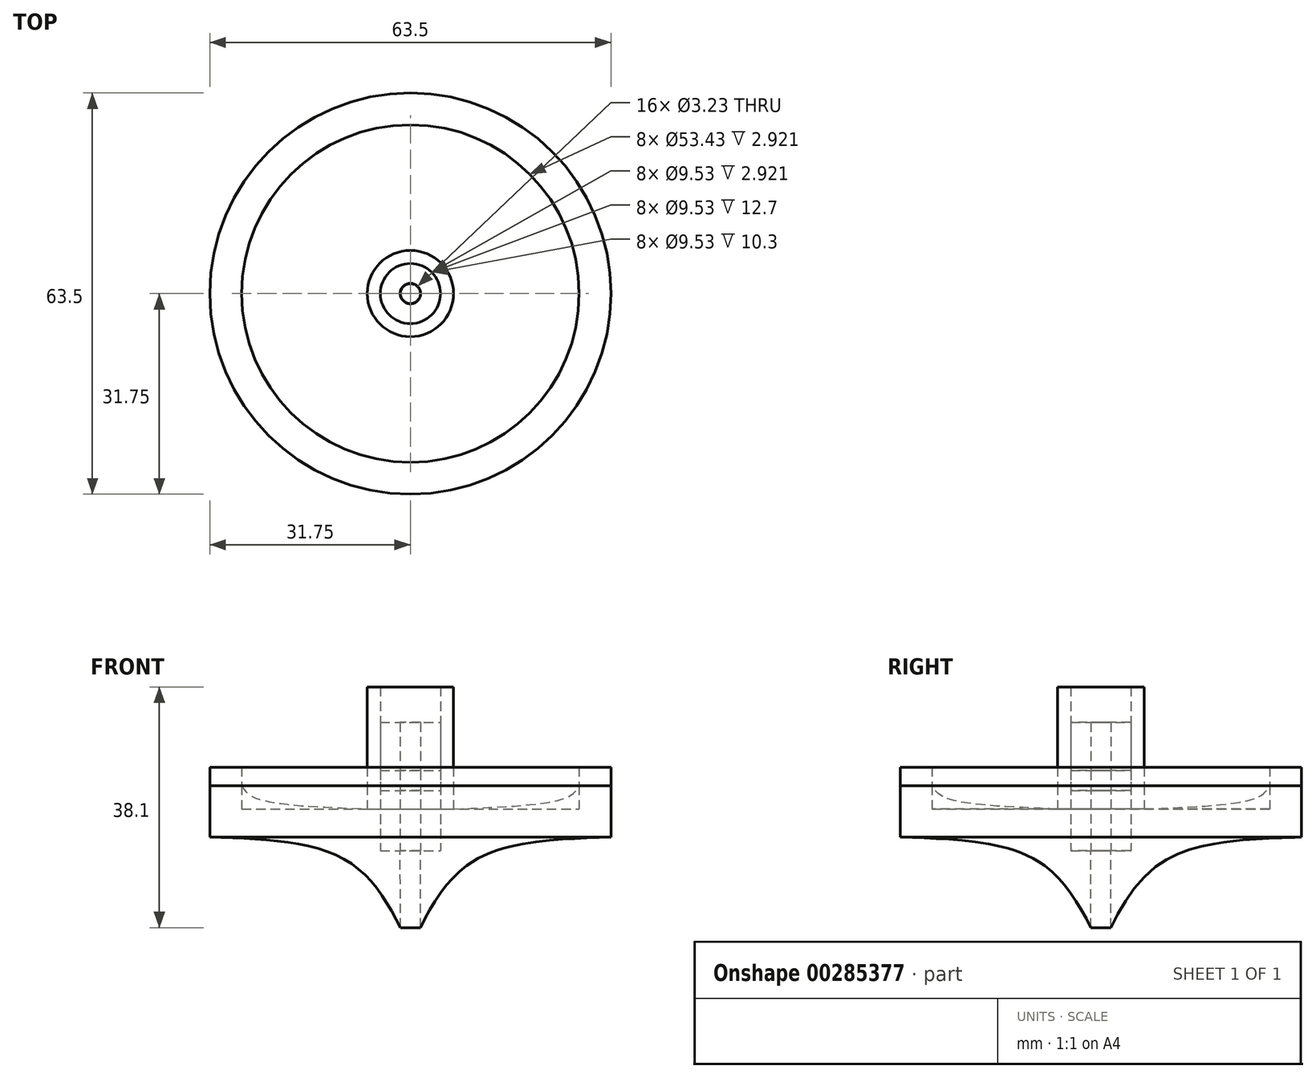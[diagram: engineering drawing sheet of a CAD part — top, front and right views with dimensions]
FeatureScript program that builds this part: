
annotation { "Feature Type Name" : "Feature", "Feature Type Description" : "" }
export const myFeature = defineFeature(function(context is Context, id is Id, definition is map)
    precondition{}
    {
        {
            var Q0;
            Q0=qCreatedBy(makeId("Front.planeOp"),FACE);
            var sketch = newSketch(context, id + "F0", { "sketchPlane" : qUnion([Q0])});
            skLineSegment(sketch, "E0", {"start": v(0, 0) * mm, "end": v(31.75, 0) * mm});
            skLineSegment(sketch, "E1", {"start": v(31.75, 0) * mm, "end": v(31.75, 8.17) * mm});
            skLineSegment(sketch, "E2", {"start": v(31.75, 8.17) * mm, "end": v(26.72, 8.17) * mm});
            skLineSegment(sketch, "E3", {"start": v(0, 8.17) * mm, "end": v(0, 0) * mm});
            skLineSegment(sketch, "E4.MirrorCS", {"start": v(-31.75, 8.17) * mm, "end": v(-26.72, 8.17) * mm});
            skLineSegment(sketch, "E5.MirrorCS", {"start": v(0, 0) * mm, "end": v(-31.75, 0) * mm});
            skLineSegment(sketch, "E6.MirrorCS", {"start": v(-31.75, 0) * mm, "end": v(-31.75, 8.17) * mm});
            skPoint(sketch, "E7", {"position": v(-26.72, 8.17) * mm});
            skPoint(sketch, "E8", {"position": v(-26.72, 4.48) * mm});
            skLineSegment(sketch, "E9", {"start": v(-26.72, 8.17) * mm, "end": v(-26.72, 4.48) * mm});
            skLineSegment(sketch, "E10", {"start": v(-26.72, 4.48) * mm, "end": v(0, 4.48) * mm});
            skPoint(sketch, "E10.endSnap0", {"position": v(0, 4.09) * mm});
            skLineSegment(sketch, "E11", {"start": v(0, 4.48) * mm, "end": v(0, 8.17) * mm});
            skLineSegment(sketch, "E12.MirrorCS", {"start": v(26.72, 4.48) * mm, "end": v(0, 4.48) * mm});
            skPoint(sketch, "E13.MirrorP", {"position": v(26.72, 4.48) * mm});
            skLineSegment(sketch, "E14.MirrorCS", {"start": v(26.72, 8.17) * mm, "end": v(26.72, 4.48) * mm});
            skPoint(sketch, "E15.orphan", {"position": v(0, 8.17) * mm});
            skLineSegment(sketch, "E16", {"start": v(0, 4.48) * mm, "end": v(6.83, 4.48) * mm});
            skLineSegment(sketch, "E17", {"start": v(6.83, 4.48) * mm, "end": v(6.83, 8.17) * mm});
            skLineSegment(sketch, "E18", {"start": v(6.83, 8.17) * mm, "end": v(4.76, 8.17) * mm});
            skLineSegment(sketch, "E19", {"start": v(0, 4.48) * mm, "end": v(4.76, 4.48) * mm});
            skLineSegment(sketch, "E20", {"start": v(4.76, 4.48) * mm, "end": v(4.76, 8.17) * mm});
            skPoint(sketch, "E21.MirrorCS.start.orphan", {"position": v(-6.83, 8.17) * mm});
            skPoint(sketch, "E22.MirrorCS.start.orphan", {"position": v(-6.83, 4.48) * mm});
            skLineSegment(sketch, "E23.MirrorCS", {"start": v(-4.76, 4.48) * mm, "end": v(-4.76, 8.17) * mm});
            skLineSegment(sketch, "E24.MirrorCS", {"start": v(-6.83, 8.17) * mm, "end": v(-4.76, 8.17) * mm});
            skLineSegment(sketch, "E25.MirrorCS", {"start": v(-6.83, 4.48) * mm, "end": v(-6.83, 8.17) * mm});
            skFitSpline(sketch, "E26", {"points": [v(-26.72, 8.17) * mm, v(-24.89, 6.38) * mm, v(-6.83, 4.48) * mm], "startDerivative": vector(4.23, -7.1) * mm, "endDerivative": vector(31.44, -1.18) * mm});
            skFitSpline(sketch, "E27.MirrorCS", {"points": [v(26.72, 8.17) * mm, v(24.89, 6.38) * mm, v(6.83, 4.48) * mm], "startDerivative": vector(-4.23, -7.1) * mm, "endDerivative": vector(-31.44, -1.18) * mm});
            skLineSegment(sketch, "E28", {"start": v(0, 0) * mm, "end": v(1.68, 0) * mm});
            skLineSegment(sketch, "E29", {"start": v(0, 0) * mm, "end": v(1.57, 0) * mm});
            skFitSpline(sketch, "E30", {"points": [v(-31.75, 0) * mm, v(-9.83, -3.86) * mm, v(0, -17.56) * mm], "startDerivative": vector(46.32, -1.28) * mm, "endDerivative": vector(16.5, -34.6) * mm});
            skFitSpline(sketch, "E31.MirrorCS", {"points": [v(31.75, 0) * mm, v(9.83, -3.86) * mm, v(0, -17.56) * mm], "startDerivative": vector(-46.32, -1.28) * mm, "endDerivative": vector(-16.5, -34.6) * mm});
            skLineSegment(sketch, "E32", {"start": v(1.57, 0) * mm, "end": v(1.62, 0) * mm});
            skLineSegment(sketch, "E33.MirrorCS", {"start": v(-1.62, 0) * mm, "end": v(-1.57, -17.56) * mm});
            skPoint(sketch, "E34", {"position": v(1.58, -14.3) * mm});
            skPoint(sketch, "E35", {"position": v(0, -14.3) * mm});
            skSolve(sketch);
        }
        {
            var Q0;
            {var subQ0=sQuery(id+"F0.wireOp",EDGE,"E9");Q0=makeQuery(id+"F0.imprint","IMPRINT",FACE,{"disambiguationData":[TD([[makeQuery(id+"F0.imprint","IMPRINT",EDGE,{"derivedFrom":subQ0}),1.0]])]});}
            var Q1;
            {var subQ0=sQuery(id+"F0.wireOp",EDGE,"E23.MirrorCS");Q1=makeQuery(id+"F0.imprint","IMPRINT",FACE,{"disambiguationData":[TD([[makeQuery(id+"F0.imprint","IMPRINT",EDGE,{"derivedFrom":subQ0}),1.0]])]});}
            var Q2;
            Q2=makeQuery(id+"F0.imprint","IMPRINT",FACE,{"disambiguationData":[TD([[makeQuery(id+"F0.imprint","IMPRINT",EDGE,{"derivedFrom":sQuery(id+"F0.wireOp",EDGE,"E12.MirrorCS")}),-1.0]])]});
            var Q3;
            Q3=makeQuery(id+"F0.imprint","IMPRINT",FACE,{"disambiguationData":[TD([[makeQuery(id+"F0.imprint","IMPRINT",EDGE,{"derivedFrom":sQuery(id+"F0.wireOp",EDGE,"E16")}),1.0]])]});
            var Q4;
            {var subQ1=sQuery(id+"F0.wireOp",EDGE,"E5.MirrorCS");var subQ3=sQuery(id+"F0.wireOp",EDGE,"E33.MirrorCS");var subQ4=makeQuery(id+"F0.imprint","INTERSECT",VERTEX,{"derivedFrom":[subQ1,subQ3]});Q4=makeQuery(id+"F0.imprint","IMPRINT",FACE,{"disambiguationData":[TD([[makeQuery(id+"F0.imprint","IMPRINT",EDGE,{"disambiguationData":[TD([[subQ4,-1.0]])],"derivedFrom":subQ3}),-1.0]])]});}
            var Q5;
            {var subQ3=sQuery(id+"F0.wireOp",EDGE,"E3");Q5=makeQuery(id+"F0.imprint","IMPRINT",FACE,{"disambiguationData":[TD([[makeQuery(id+"F0.imprint","IMPRINT",EDGE,{"derivedFrom":subQ3}),-1.0]])]});}
            var Q6;
            Q6=sQuery(id+"F0.wireOp",EDGE,"E11");
            revolve(context, id + "F1", {"entities" : qUnion([Q0, Q1, Q2, Q3, Q4, Q5]), "axis" : qUnion([Q6]), "revolveType" : RevolveType.FULL});
        }
        {
            var Q0;
            Q0=makeQuery(id+"F1.opRevolve","SWEPT_FACE",FACE,{"disambiguationData":[OSD([sQuery(id+"F0.wireOp",EDGE,"E4.MirrorCS")])]});
            var Q1;
            Q1=makeQuery(id+"F1.opRevolve","SWEPT_FACE",FACE,{"disambiguationData":[OSD([sQuery(id+"F0.wireOp",EDGE,"E24.MirrorCS")])]});
            var Q2;
            Q2=makeQuery(id+"F1.opRevolve","SWEPT_FACE",FACE,{"disambiguationData":[OSD([sQuery(id+"F0.wireOp",EDGE,"E10")])]});
            extrude(context, id + "F2", {"entities" : qUnion([Q0, Q1, Q2]), "depth" : 2.92 * mm});
        }
        {
            var Q0;
            Q0=makeQuery(id+"F2.opExtrude","CAP_FACE",FACE,{"disambiguationData":[OSD([sQuery(id+"F0.wireOp",EDGE,"E10")])],"isStart":false});
            extrude(context, id + "F3", {"entities" : qUnion([Q0]), "operationType" : NewBodyOperationType.REMOVE, "oppositeDirection" : true, "depth" : 9.52 * mm});
        }
        {
            var Q0;
            Q0=makeQuery(id+"F2.opExtrude","CAP_FACE",FACE,{"disambiguationData":[OSD([sQuery(id+"F0.wireOp",EDGE,"E24.MirrorCS")])],"isStart":false});
            var Q1;
            Q1=makeQuery(id+"F3.boolean.opBoolean","COPY",FACE,{"derivedFrom":makeQuery(id+"F3.opExtrude","CAP_FACE",FACE,{"disambiguationData":[OSD([sQuery(id+"F0.wireOp",EDGE,"E10")])],"isStart":false})});
            extrude(context, id + "F4", {"entities" : qUnion([Q0, Q1]), "depth" : 12.7 * mm});
        }
        {
            var Q0;
            Q0=makeQuery(id+"F4.opExtrude","CAP_FACE",FACE,{"disambiguationData":[OSD([sQuery(id+"F0.wireOp",EDGE,"E10")])],"isStart":false});
            extrude(context, id + "F5", {"entities" : qUnion([Q0]), "depth" : 7.62 * mm});
        }
    });
